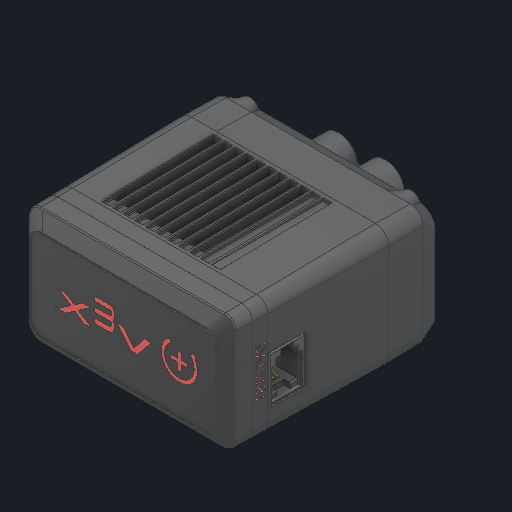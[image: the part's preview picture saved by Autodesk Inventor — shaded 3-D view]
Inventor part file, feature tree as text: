
AUTODESK INVENTOR PART (.ipt)
format: ipt  version: 2024 (Build 280153000, 153)  size: 13,035,520 bytes
history: native  units: in
note: dims shown in document units (in); Inventor stores cm internally (conversion verified against a paired STEP export)
features: other x19, sketch x2
ambient origin geometry x8: Origin, YZ Plane, XZ Plane, XY Plane, X Axis, Y Axis, Z Axis, Center Point
bodies: Solid1 (feature_tree), Solid2 (feature_tree), Solid7 (feature_tree), Solid8 (feature_tree), Solid9 (feature_tree), Solid20 (feature_tree), Solid21 (feature_tree), Solid22 (feature_tree)
feature tree (21):
  other  "V5 Motor.ipt"
  other  "Solid1::V5 Motor.ipt"
  other  "Solid2::V5 Motor.ipt"
  other  "Solid4::V5 Motor.ipt"
  other  "Solid6::V5 Motor.ipt"
  other  "Solid7::V5 Motor.ipt"
  other  "Solid8::V5 Motor.ipt"
  other  "Solid9::V5 Motor.ipt"
  other  "Solid14::V5 Motor.ipt"
  other  "Solid16::V5 Motor.ipt"
  other  "Solid17::V5 Motor.ipt"
  other  "Solid18::V5 Motor.ipt"
  other  "Solid19::V5 Motor.ipt"
  other  "Solid20::V5 Motor.ipt"
  other  "Solid21::V5 Motor.ipt"
  other  "Solid22::V5 Motor.ipt"
  other  "TaggingFeature1"
  sketch  "Sketch1"  dims[d0=0.3937in]
  sketch  "Sketch2"  dims[d4=0.0in d5=0.0in]
  other  "iInsert:1"
  other  "iInsert:2"
